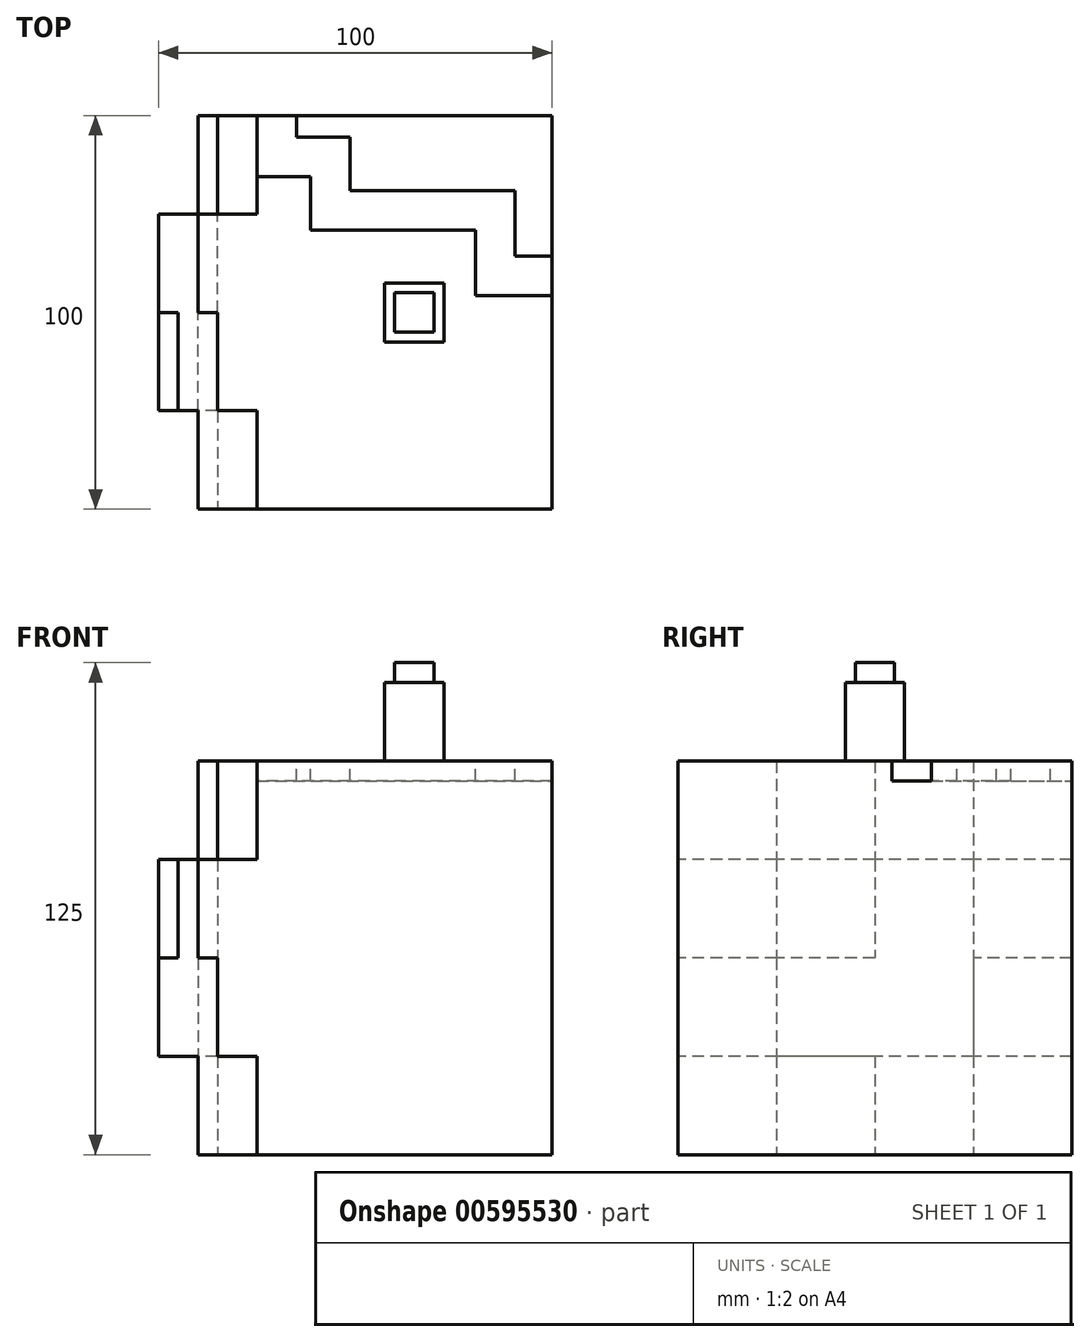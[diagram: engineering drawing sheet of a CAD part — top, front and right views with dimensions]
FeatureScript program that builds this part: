
annotation { "Feature Type Name" : "Feature", "Feature Type Description" : "" }
export const myFeature = defineFeature(function(context is Context, id is Id, definition is map)
    precondition{}
    {
        {
            var Q0;
            Q0=qCreatedBy(makeId("Top.planeOp"),FACE);
            var sketch = newSketch(context, id + "F0", { "sketchPlane" : qUnion([Q0])});
            skLineSegment(sketch, "E0.bottom", {"start": v(51.35, -50) * mm, "end": v(-48.65, -50) * mm});
            skLineSegment(sketch, "E0.top", {"start": v(51.35, 50) * mm, "end": v(-48.65, 50) * mm});
            skLineSegment(sketch, "E0.left", {"start": v(51.35, -50) * mm, "end": v(51.35, 50) * mm});
            skLineSegment(sketch, "E0.right", {"start": v(-48.65, -50) * mm, "end": v(-48.65, 50) * mm});
            skPoint(sketch, "E0.middle", {"position": v(1.35, 0) * mm});
            skSolve(sketch);
        }
        {
            var Q0;
            Q0=makeQuery(id+"F0.imprint","IMPRINT",FACE,{"disambiguationData":[TD([[makeQuery(id+"F0.imprint","IMPRINT",EDGE,{"derivedFrom":sQuery(id+"F0.wireOp",EDGE,"E0.bottom")}),-1.0]])]});
            extrude(context, id + "F1", {"entities" : qUnion([Q0]), "depth" : 100 * mm, "offsetDistance" : 25 * mm});
        }
        {
            var Q0;
            Q0=makeQuery(id+"F1.opExtrude","SWEPT_FACE",FACE,{"disambiguationData":[OSD([sQuery(id+"F0.wireOp",EDGE,"E0.right")])]});
            var sketch = newSketch(context, id + "F2", { "sketchPlane" : qUnion([Q0])});
            skLineSegment(sketch, "E1", {"start": v(0, 100) * mm, "end": v(0, 0) * mm});
            skLineSegment(sketch, "E2", {"start": v(-50, 50) * mm, "end": v(50, 50) * mm});
            skLineSegment(sketch, "E3", {"start": v(-50, 75) * mm, "end": v(50, 75) * mm});
            skLineSegment(sketch, "E4", {"start": v(-50, 25) * mm, "end": v(50, 25) * mm});
            skLineSegment(sketch, "E5", {"start": v(-25, 100) * mm, "end": v(-25, 0) * mm});
            skLineSegment(sketch, "E6", {"start": v(25, 100) * mm, "end": v(25, 0) * mm});
            skSolve(sketch);
        }
        {
            var Q0;
            {var subQ1=sQuery(id+"F0.wireOp",EDGE,"E0.right");var subQ4=sQuery(id+"F2.wireOp",EDGE,"E5");var subQ6=makeQuery(id+"F1.opExtrude","CAP_EDGE",EDGE,{"disambiguationData":[OSD([subQ1])],"isStart":false});var subQ7=makeQuery(id+"F2.imprint","INTERSECT",VERTEX,{"derivedFrom":[subQ6,subQ4]});Q0=makeQuery(id+"F2.imprint","IMPRINT",FACE,{"disambiguationData":[TD([[makeQuery(id+"F2.imprint","IMPRINT",EDGE,{"disambiguationData":[TD([[subQ7,-1.0]])],"derivedFrom":subQ4}),-1.0]])]});}
            var Q1;
            {var subQ1=sQuery(id+"F0.wireOp",EDGE,"E0.right");var subQ4=sQuery(id+"F2.wireOp",EDGE,"E5");var subQ6=makeQuery(id+"F1.opExtrude","CAP_EDGE",EDGE,{"disambiguationData":[OSD([subQ1])],"isStart":true});var subQ7=makeQuery(id+"F2.imprint","INTERSECT",VERTEX,{"derivedFrom":[subQ6,subQ4]});Q1=makeQuery(id+"F2.imprint","IMPRINT",FACE,{"disambiguationData":[TD([[makeQuery(id+"F2.imprint","IMPRINT",EDGE,{"disambiguationData":[TD([[subQ7,1.0]])],"derivedFrom":subQ4}),-1.0]])]});}
            var Q2;
            {var subQ1=sQuery(id+"F0.wireOp",EDGE,"E0.right");var subQ4=sQuery(id+"F2.wireOp",EDGE,"E6");var subQ6=makeQuery(id+"F1.opExtrude","CAP_EDGE",EDGE,{"disambiguationData":[OSD([subQ1])],"isStart":true});var subQ7=makeQuery(id+"F2.imprint","INTERSECT",VERTEX,{"derivedFrom":[subQ6,subQ4]});Q2=makeQuery(id+"F2.imprint","IMPRINT",FACE,{"disambiguationData":[TD([[makeQuery(id+"F2.imprint","IMPRINT",EDGE,{"disambiguationData":[TD([[subQ7,1.0]])],"derivedFrom":subQ4}),1.0]])]});}
            var Q3;
            {var subQ1=sQuery(id+"F0.wireOp",EDGE,"E0.right");var subQ4=sQuery(id+"F2.wireOp",EDGE,"E6");var subQ6=makeQuery(id+"F1.opExtrude","CAP_EDGE",EDGE,{"disambiguationData":[OSD([subQ1])],"isStart":false});var subQ8=makeQuery(id+"F2.imprint","INTERSECT",VERTEX,{"derivedFrom":[subQ6,subQ4]});Q3=makeQuery(id+"F2.imprint","IMPRINT",FACE,{"disambiguationData":[TD([[makeQuery(id+"F2.imprint","IMPRINT",EDGE,{"disambiguationData":[TD([[subQ8,-1.0]])],"derivedFrom":subQ4}),1.0]])]});}
            extrude(context, id + "F3", {"entities" : qUnion([Q0, Q1, Q2, Q3]), "operationType" : NewBodyOperationType.REMOVE, "oppositeDirection" : true, "depth" : 25 * mm, "offsetDistance" : 25 * mm});
        }
        {
            var Q0;
            {var subQ0=sQuery(id+"F2.wireOp",EDGE,"E2");var subQ3=sQuery(id+"F2.wireOp",EDGE,"E5");var subQ4=makeQuery(id+"F2.imprint","INTERSECT",VERTEX,{"derivedFrom":[subQ0,subQ3]});Q0=makeQuery(id+"F2.imprint","IMPRINT",FACE,{"disambiguationData":[TD([[makeQuery(id+"F2.imprint","IMPRINT",EDGE,{"disambiguationData":[TD([[subQ4,1.0]])],"derivedFrom":subQ3}),-1.0]])]});}
            var Q1;
            {var subQ0=sQuery(id+"F2.wireOp",EDGE,"E2");var subQ3=sQuery(id+"F2.wireOp",EDGE,"E6");var subQ4=makeQuery(id+"F2.imprint","INTERSECT",VERTEX,{"derivedFrom":[subQ0,subQ3]});Q1=makeQuery(id+"F2.imprint","IMPRINT",FACE,{"disambiguationData":[TD([[makeQuery(id+"F2.imprint","IMPRINT",EDGE,{"disambiguationData":[TD([[subQ4,-1.0]])],"derivedFrom":subQ3}),1.0]])]});}
            var Q2;
            {var subQ0=sQuery(id+"F2.wireOp",EDGE,"E1");var subQ1=makeQuery(id+"F1.opExtrude","CAP_EDGE",EDGE,{"disambiguationData":[OSD([sQuery(id+"F0.wireOp",EDGE,"E0.right")])],"isStart":false});var subQ2=makeQuery(id+"F2.imprint","INTERSECT",VERTEX,{"derivedFrom":[subQ1,subQ0]});Q2=makeQuery(id+"F2.imprint","IMPRINT",FACE,{"disambiguationData":[TD([[makeQuery(id+"F2.imprint","IMPRINT",EDGE,{"disambiguationData":[TD([[subQ2,-1.0]])],"derivedFrom":subQ0}),1.0]])]});}
            var Q3;
            {var subQ0=sQuery(id+"F2.wireOp",EDGE,"E1");var subQ1=makeQuery(id+"F1.opExtrude","CAP_EDGE",EDGE,{"disambiguationData":[OSD([sQuery(id+"F0.wireOp",EDGE,"E0.right")])],"isStart":true});var subQ2=makeQuery(id+"F2.imprint","INTERSECT",VERTEX,{"derivedFrom":[subQ1,subQ0]});Q3=makeQuery(id+"F2.imprint","IMPRINT",FACE,{"disambiguationData":[TD([[makeQuery(id+"F2.imprint","IMPRINT",EDGE,{"disambiguationData":[TD([[subQ2,1.0]])],"derivedFrom":subQ0}),-1.0]])]});}
            extrude(context, id + "F4", {"entities" : qUnion([Q0, Q1, Q2, Q3]), "operationType" : NewBodyOperationType.REMOVE, "oppositeDirection" : true, "depth" : 15 * mm, "offsetDistance" : 25 * mm});
        }
        {
            var Q0;
            {var subQ0=sQuery(id+"F2.wireOp",EDGE,"E1");var subQ1=makeQuery(id+"F1.opExtrude","CAP_EDGE",EDGE,{"disambiguationData":[OSD([sQuery(id+"F0.wireOp",EDGE,"E0.right")])],"isStart":false});var subQ2=makeQuery(id+"F2.imprint","INTERSECT",VERTEX,{"derivedFrom":[subQ1,subQ0]});Q0=makeQuery(id+"F2.imprint","IMPRINT",FACE,{"disambiguationData":[TD([[makeQuery(id+"F2.imprint","IMPRINT",EDGE,{"disambiguationData":[TD([[subQ2,-1.0]])],"derivedFrom":subQ0}),-1.0]])]});}
            var Q1;
            {var subQ0=sQuery(id+"F2.wireOp",EDGE,"E1");var subQ1=makeQuery(id+"F1.opExtrude","CAP_EDGE",EDGE,{"disambiguationData":[OSD([sQuery(id+"F0.wireOp",EDGE,"E0.right")])],"isStart":true});var subQ2=makeQuery(id+"F2.imprint","INTERSECT",VERTEX,{"derivedFrom":[subQ1,subQ0]});Q1=makeQuery(id+"F2.imprint","IMPRINT",FACE,{"disambiguationData":[TD([[makeQuery(id+"F2.imprint","IMPRINT",EDGE,{"disambiguationData":[TD([[subQ2,1.0]])],"derivedFrom":subQ0}),1.0]])]});}
            var Q2;
            {var subQ0=sQuery(id+"F2.wireOp",EDGE,"E2");var subQ3=sQuery(id+"F2.wireOp",EDGE,"E5");var subQ4=makeQuery(id+"F2.imprint","INTERSECT",VERTEX,{"derivedFrom":[subQ0,subQ3]});Q2=makeQuery(id+"F2.imprint","IMPRINT",FACE,{"disambiguationData":[TD([[makeQuery(id+"F2.imprint","IMPRINT",EDGE,{"disambiguationData":[TD([[subQ4,-1.0]])],"derivedFrom":subQ3}),-1.0]])]});}
            var Q3;
            {var subQ0=sQuery(id+"F2.wireOp",EDGE,"E2");var subQ3=sQuery(id+"F2.wireOp",EDGE,"E6");var subQ4=makeQuery(id+"F2.imprint","INTERSECT",VERTEX,{"derivedFrom":[subQ0,subQ3]});Q3=makeQuery(id+"F2.imprint","IMPRINT",FACE,{"disambiguationData":[TD([[makeQuery(id+"F2.imprint","IMPRINT",EDGE,{"disambiguationData":[TD([[subQ4,1.0]])],"derivedFrom":subQ3}),1.0]])]});}
            extrude(context, id + "F5", {"entities" : qUnion([Q0, Q1, Q2, Q3]), "operationType" : NewBodyOperationType.REMOVE, "oppositeDirection" : true, "depth" : 10 * mm, "offsetDistance" : 25 * mm});
        }
        {
            var Q0;
            {var subQ0=sQuery(id+"F2.wireOp",EDGE,"E3");var subQ1=sQuery(id+"F2.wireOp",EDGE,"E1");var subQ2=makeQuery(id+"F2.imprint","INTERSECT",VERTEX,{"derivedFrom":[subQ1,subQ0]});Q0=makeQuery(id+"F2.imprint","IMPRINT",FACE,{"disambiguationData":[TD([[makeQuery(id+"F2.imprint","IMPRINT",EDGE,{"disambiguationData":[TD([[subQ2,-1.0]])],"derivedFrom":subQ1}),1.0]])]});}
            extrude(context, id + "F6", {"entities" : qUnion([Q0]), "operationType" : NewBodyOperationType.REMOVE, "oppositeDirection" : true, "depth" : 5 * mm, "offsetDistance" : 25 * mm});
        }
        {
            var Q0;
            Q0=makeQuery(id+"F1.opExtrude","CAP_FACE",FACE,{"disambiguationData":[OSD([sQuery(id+"F0.wireOp",EDGE,"E0.bottom"),sQuery(id+"F0.wireOp",EDGE,"E0.top"),sQuery(id+"F0.wireOp",EDGE,"E0.left"),sQuery(id+"F0.wireOp",EDGE,"E0.right")])],"isStart":false});
            var sketch = newSketch(context, id + "F7", { "sketchPlane" : qUnion([Q0])});
            skLineSegment(sketch, "E7", {"start": v(51.35, 50) * mm, "end": v(-23.65, 50) * mm});
            skLineSegment(sketch, "E8", {"start": v(-23.65, 50) * mm, "end": v(-23.65, 34.5) * mm});
            skLineSegment(sketch, "E9", {"start": v(-23.65, 34.5) * mm, "end": v(-10, 34.5) * mm});
            skLineSegment(sketch, "E10", {"start": v(-10, 34.5) * mm, "end": v(-10, 20.88) * mm});
            skLineSegment(sketch, "E11", {"start": v(-10, 20.88) * mm, "end": v(31.88, 20.88) * mm});
            skLineSegment(sketch, "E12", {"start": v(31.88, 20.88) * mm, "end": v(31.88, 4.3) * mm});
            skLineSegment(sketch, "E13", {"start": v(31.88, 4.3) * mm, "end": v(51.35, 4.3) * mm});
            skLineSegment(sketch, "E14", {"start": v(51.35, 4.3) * mm, "end": v(51.35, 14.3) * mm});
            skLineSegment(sketch, "E15", {"start": v(51.35, 14.3) * mm, "end": v(41.88, 14.3) * mm});
            skLineSegment(sketch, "E16", {"start": v(41.88, 14.3) * mm, "end": v(41.88, 30.88) * mm});
            skLineSegment(sketch, "E17", {"start": v(41.88, 30.88) * mm, "end": v(0, 30.88) * mm});
            skLineSegment(sketch, "E18", {"start": v(0, 30.88) * mm, "end": v(0, 44.5) * mm});
            skLineSegment(sketch, "E19", {"start": v(0, 44.5) * mm, "end": v(-13.65, 44.5) * mm});
            skLineSegment(sketch, "E20", {"start": v(-13.65, 44.5) * mm, "end": v(-13.65, 50) * mm});
            skLineSegment(sketch, "E21", {"start": v(-13.65, 50) * mm, "end": v(-23.65, 50) * mm});
            skSolve(sketch);
        }
        {
            var Q0;
            Q0=makeQuery(id+"F7.imprint","IMPRINT",FACE,{"disambiguationData":[TD([[makeQuery(id+"F7.imprint","IMPRINT",EDGE,{"derivedFrom":sQuery(id+"F7.wireOp",EDGE,"E8")}),-1.0]])]});
            extrude(context, id + "F8", {"entities" : qUnion([Q0]), "operationType" : NewBodyOperationType.REMOVE, "oppositeDirection" : true, "depth" : 5 * mm, "offsetDistance" : 25 * mm});
        }
        {
            var Q0;
            {var subQ5=sQuery(id+"F0.wireOp",EDGE,"E0.right");var subQ8=sQuery(id+"F0.wireOp",EDGE,"E0.bottom");var subQ9=sQuery(id+"F0.wireOp",EDGE,"E0.top");var subQ10=sQuery(id+"F0.wireOp",EDGE,"E0.left");Q0=makeQuery(id+"F8.boolean.opBoolean","SPLIT",FACE,{"disambiguationData":[TD([makeQuery(id+"F1.opExtrude","SWEPT_FACE",FACE,{"disambiguationData":[OSD([subQ8])]})])],"derivedFrom":makeQuery(id+"F1.opExtrude","CAP_FACE",FACE,{"disambiguationData":[OSD([subQ8,subQ9,subQ10,subQ5])],"isStart":false})});}
            var sketch = newSketch(context, id + "F9", { "sketchPlane" : qUnion([Q0])});
            skLineSegment(sketch, "E22.bottom", {"start": v(8.8, 7.5) * mm, "end": v(23.8, 7.5) * mm});
            skLineSegment(sketch, "E22.top", {"start": v(8.8, -7.5) * mm, "end": v(23.8, -7.5) * mm});
            skLineSegment(sketch, "E22.left", {"start": v(8.8, 7.5) * mm, "end": v(8.8, -7.5) * mm});
            skLineSegment(sketch, "E22.right", {"start": v(23.8, 7.5) * mm, "end": v(23.8, -7.5) * mm});
            skPoint(sketch, "E22.middle", {"position": v(16.3, 0) * mm});
            skSolve(sketch);
        }
        {
            var Q0;
            Q0=makeQuery(id+"F9.imprint","IMPRINT",FACE,{"disambiguationData":[TD([[makeQuery(id+"F9.imprint","IMPRINT",EDGE,{"derivedFrom":sQuery(id+"F9.wireOp",EDGE,"E22.bottom")}),-1.0]])]});
            extrude(context, id + "F10", {"entities" : qUnion([Q0]), "operationType" : NewBodyOperationType.ADD, "depth" : 20 * mm, "offsetDistance" : 25 * mm});
        }
        {
            var Q0;
            Q0=makeQuery(id+"F10.opExtrude","CAP_FACE",FACE,{"disambiguationData":[OSD([sQuery(id+"F9.wireOp",EDGE,"E22.bottom"),sQuery(id+"F9.wireOp",EDGE,"E22.top"),sQuery(id+"F9.wireOp",EDGE,"E22.left"),sQuery(id+"F9.wireOp",EDGE,"E22.right")])],"isStart":false});
            var sketch = newSketch(context, id + "F11", { "sketchPlane" : qUnion([Q0])});
            skLineSegment(sketch, "E23.bottom", {"start": v(21.3, -5) * mm, "end": v(11.3, -5) * mm});
            skLineSegment(sketch, "E23.top", {"start": v(21.3, 5) * mm, "end": v(11.3, 5) * mm});
            skLineSegment(sketch, "E23.left", {"start": v(21.3, -5) * mm, "end": v(21.3, 5) * mm});
            skLineSegment(sketch, "E23.right", {"start": v(11.3, -5) * mm, "end": v(11.3, 5) * mm});
            skPoint(sketch, "E23.middle", {"position": v(16.3, 0) * mm});
            skSolve(sketch);
        }
        {
            var Q0;
            Q0=makeQuery(id+"F11.imprint","IMPRINT",FACE,{"disambiguationData":[TD([[makeQuery(id+"F11.imprint","IMPRINT",EDGE,{"derivedFrom":sQuery(id+"F11.wireOp",EDGE,"E23.bottom")}),-1.0]])]});
            extrude(context, id + "F12", {"entities" : qUnion([Q0]), "operationType" : NewBodyOperationType.ADD, "depth" : 5 * mm, "offsetDistance" : 25 * mm});
        }
    });
